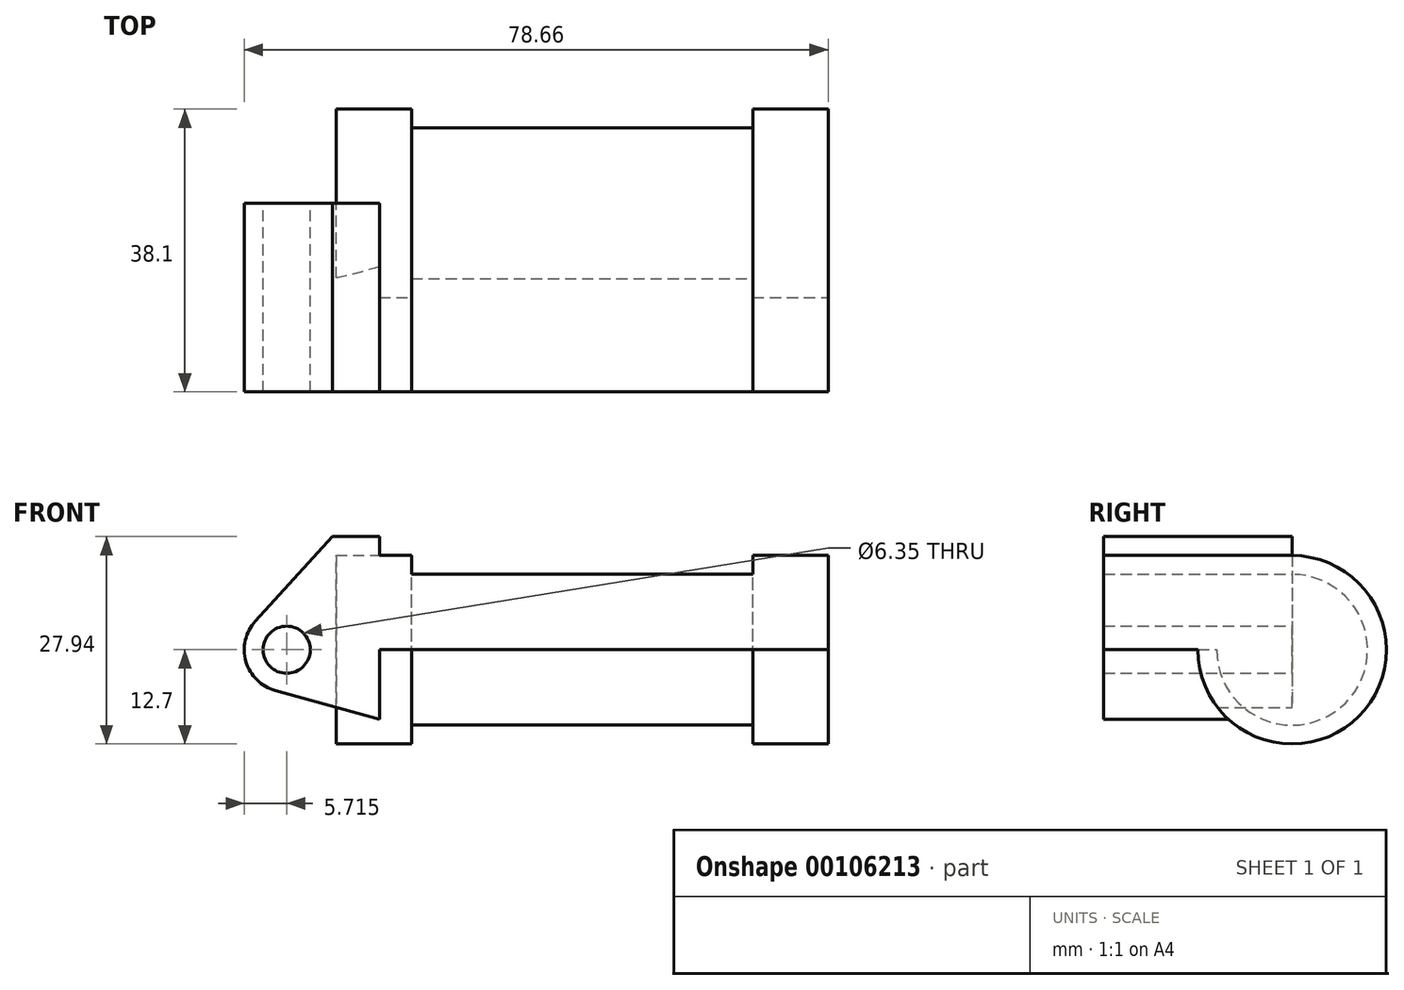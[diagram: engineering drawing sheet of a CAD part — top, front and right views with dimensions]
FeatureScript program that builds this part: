
annotation { "Feature Type Name" : "Feature", "Feature Type Description" : "" }
export const myFeature = defineFeature(function(context is Context, id is Id, definition is map)
    precondition{}
    {
        {
            var Q0;
            Q0=qCreatedBy(makeId("Front.planeOp"),FACE);
            var sketch = newSketch(context, id + "F0", { "sketchPlane" : qUnion([Q0])});
            skLineSegment(sketch, "E0", {"start": v(0, 0) * mm, "end": v(0, 12.7) * mm});
            skLineSegment(sketch, "E1", {"start": v(0, 12.7) * mm, "end": v(10.16, 12.7) * mm});
            skLineSegment(sketch, "E2", {"start": v(10.16, 12.7) * mm, "end": v(10.16, 10.16) * mm});
            skLineSegment(sketch, "E3", {"start": v(10.16, 10.16) * mm, "end": v(56.13, 10.16) * mm});
            skLineSegment(sketch, "E4", {"start": v(56.13, 10.16) * mm, "end": v(56.13, 12.7) * mm});
            skLineSegment(sketch, "E5", {"start": v(56.13, 12.7) * mm, "end": v(66.3, 12.7) * mm});
            skLineSegment(sketch, "E6", {"start": v(66.3, 12.7) * mm, "end": v(66.3, 0) * mm});
            skLineSegment(sketch, "E7", {"start": v(66.3, 0) * mm, "end": v(0, 0) * mm});
            skLineSegment(sketch, "E8", {"start": v(5.84, 15.24) * mm, "end": v(-0.5, 15.24) * mm});
            skLineSegment(sketch, "E9", {"start": v(-0.5, 15.24) * mm, "end": v(-10.88, 3.85) * mm});
            skLineSegment(sketch, "E10", {"start": v(0, 0) * mm, "end": v(-6.65, 0) * mm});
            skCircle(sketch, "E11", {"center": v(-6.65, 0) * mm, "radius": 5.72 * mm});
            skCircle(sketch, "E12", {"center": v(-6.65, 0) * mm, "radius": 3.18 * mm});
            skLineSegment(sketch, "E13", {"start": v(5.84, 15.24) * mm, "end": v(5.84, -9.4) * mm});
            skLineSegment(sketch, "E14", {"start": v(5.84, -9.4) * mm, "end": v(-8.18, -5.5) * mm});
            skSolve(sketch);
        }
        {
            var Q0;
            {var subQ0=sQuery(id+"F0.wireOp",EDGE,"E2");Q0=makeQuery(id+"F0.imprint","IMPRINT",FACE,{"disambiguationData":[TD([[makeQuery(id+"F0.imprint","IMPRINT",EDGE,{"derivedFrom":subQ0}),-1.0]])]});}
            var Q1;
            {var subQ0=sQuery(id+"F0.wireOp",EDGE,"E0");Q1=makeQuery(id+"F0.imprint","IMPRINT",FACE,{"disambiguationData":[TD([[makeQuery(id+"F0.imprint","IMPRINT",EDGE,{"derivedFrom":subQ0}),-1.0]])]});}
            var Q2;
            Q2=sQuery(id+"F0.wireOp",EDGE,"E7");
            revolve(context, id + "F1", {"entities" : qUnion([Q0, Q1]), "axis" : qUnion([Q2]), "revolveType" : RevolveType.FULL});
        }
        {
            var Q0;
            Q0 = qSketchRegion(id + "F0", true);
            extrude(context, id + "F2", {"entities" : qUnion([Q0]), "operationType" : NewBodyOperationType.ADD, "depth" : 25.4 * mm});
        }
    });
